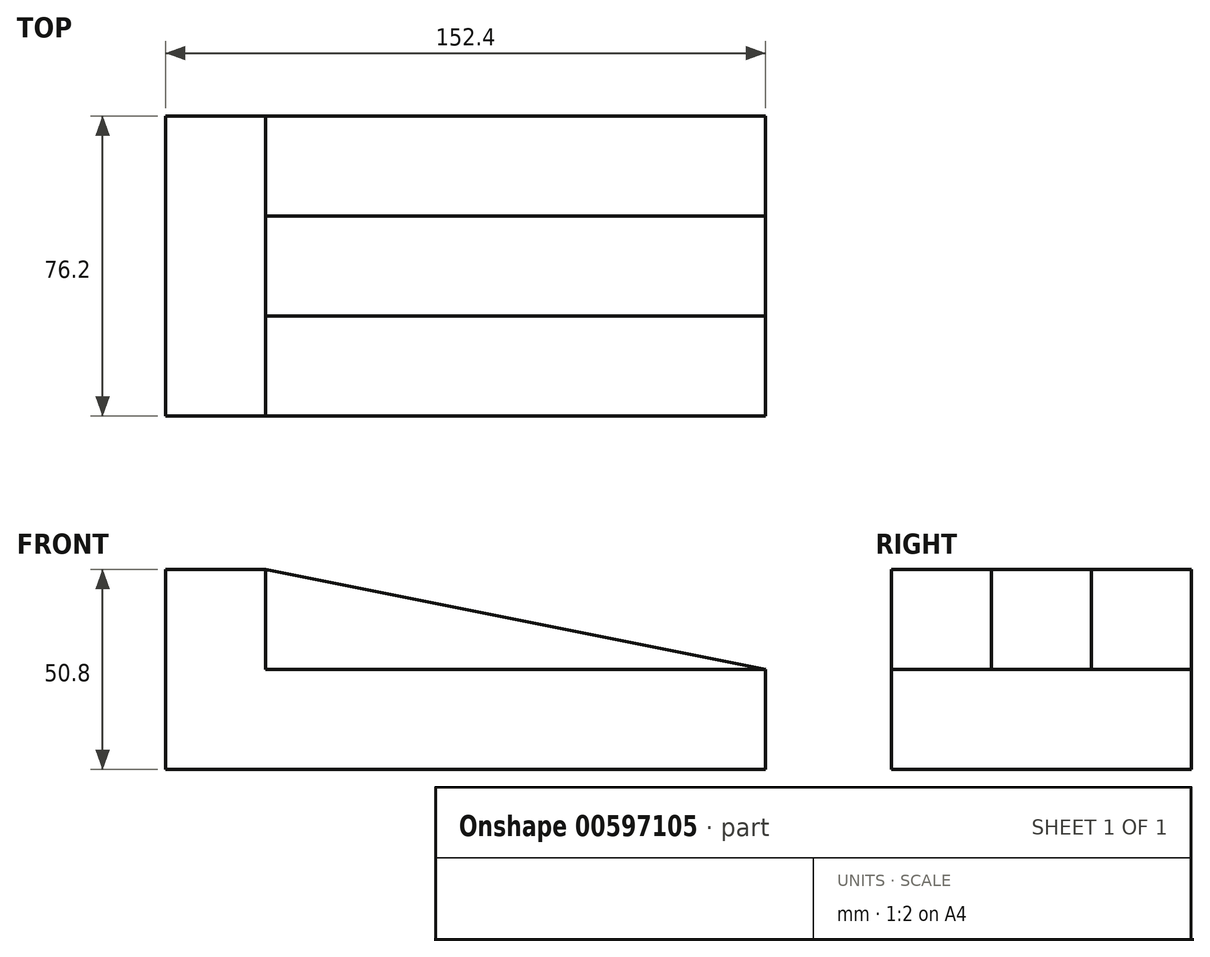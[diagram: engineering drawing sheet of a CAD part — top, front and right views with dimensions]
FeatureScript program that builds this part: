
annotation { "Feature Type Name" : "Feature", "Feature Type Description" : "" }
export const myFeature = defineFeature(function(context is Context, id is Id, definition is map)
    precondition{}
    {
        {
            var Q0;
            Q0=qCreatedBy(makeId("Front.planeOp"),FACE);
            var sketch = newSketch(context, id + "F0", { "sketchPlane" : qUnion([Q0])});
            skLineSegment(sketch, "E0.bottom", {"start": v(0, 0) * mm, "end": v(152.4, 0) * mm});
            skLineSegment(sketch, "E0.top", {"start": v(0, 50.8) * mm, "end": v(152.4, 50.8) * mm});
            skLineSegment(sketch, "E0.left", {"start": v(0, 0) * mm, "end": v(0, 50.8) * mm});
            skLineSegment(sketch, "E0.right", {"start": v(152.4, 0) * mm, "end": v(152.4, 50.8) * mm});
            skSolve(sketch);
        }
        {
            var Q0;
            Q0=makeQuery(id+"F0.imprint","IMPRINT",FACE,{"disambiguationData":[TD([[makeQuery(id+"F0.imprint","IMPRINT",EDGE,{"derivedFrom":sQuery(id+"F0.wireOp",EDGE,"E0.bottom")}),1.0]])]});
            extrude(context, id + "F1", {"entities" : qUnion([Q0]), "oppositeDirection" : true, "depth" : 76.2 * mm, "offsetDistance" : 25.4 * mm});
        }
        {
            var Q0;
            Q0=makeQuery(id+"F1.opExtrude","SWEPT_FACE",FACE,{"disambiguationData":[OSD([sQuery(id+"F0.wireOp",EDGE,"E0.top")])]});
            var sketch = newSketch(context, id + "F2", { "sketchPlane" : qUnion([Q0])});
            skLineSegment(sketch, "E1", {"start": v(152.4, 0) * mm, "end": v(152.4, 25.4) * mm});
            skLineSegment(sketch, "E2", {"start": v(152.4, 25.4) * mm, "end": v(25.4, 25.4) * mm});
            skLineSegment(sketch, "E3", {"start": v(25.4, 25.4) * mm, "end": v(25.4, 50.8) * mm});
            skLineSegment(sketch, "E4", {"start": v(25.4, 50.8) * mm, "end": v(152.4, 50.8) * mm});
            skLineSegment(sketch, "E5", {"start": v(152.4, 50.8) * mm, "end": v(152.4, 76.2) * mm});
            skLineSegment(sketch, "E6", {"start": v(25.4, 0) * mm, "end": v(25.4, 76.2) * mm});
            skSolve(sketch);
        }
        {
            var Q0;
            {var subQ0=sQuery(id+"F2.wireOp",EDGE,"E1");Q0=makeQuery(id+"F2.imprint","IMPRINT",FACE,{"disambiguationData":[TD([[makeQuery(id+"F2.imprint","IMPRINT",EDGE,{"derivedFrom":subQ0}),-1.0]])]});}
            extrude(context, id + "F3", {"entities" : qUnion([Q0]), "operationType" : NewBodyOperationType.REMOVE, "oppositeDirection" : true, "depth" : 25.4 * mm, "offsetDistance" : 25.4 * mm});
        }
        {
            var Q0;
            {var subQ0=sQuery(id+"F2.wireOp",EDGE,"E4");Q0=makeQuery(id+"F2.imprint","IMPRINT",FACE,{"disambiguationData":[TD([[makeQuery(id+"F2.imprint","IMPRINT",EDGE,{"derivedFrom":subQ0}),1.0]])]});}
            extrude(context, id + "F4", {"entities" : qUnion([Q0]), "operationType" : NewBodyOperationType.REMOVE, "oppositeDirection" : true, "depth" : 25.4 * mm, "offsetDistance" : 25.4 * mm});
        }
        {
            var Q0;
            Q0=makeQuery(id+"F3.boolean.opBoolean","COPY",FACE,{"derivedFrom":makeQuery(id+"F3.opExtrude","SWEPT_FACE",FACE,{"disambiguationData":[OSD([sQuery(id+"F2.wireOp",EDGE,"E2")])]})});
            var sketch = newSketch(context, id + "F5", { "sketchPlane" : qUnion([Q0])});
            skLineSegment(sketch, "E7", {"start": v(25.4, 50.8) * mm, "end": v(152.4, 25.4) * mm});
            skSolve(sketch);
        }
        {
            var Q0;
            Q0=makeQuery(id+"F5.imprint","IMPRINT",FACE,{"disambiguationData":[TD([[makeQuery(id+"F5.imprint","IMPRINT",EDGE,{"derivedFrom":sQuery(id+"F5.wireOp",EDGE,"E7")}),1.0]])]});
            extrude(context, id + "F6", {"entities" : qUnion([Q0]), "operationType" : NewBodyOperationType.REMOVE, "oppositeDirection" : true, "depth" : 25.4 * mm, "offsetDistance" : 25.4 * mm});
        }
    });
